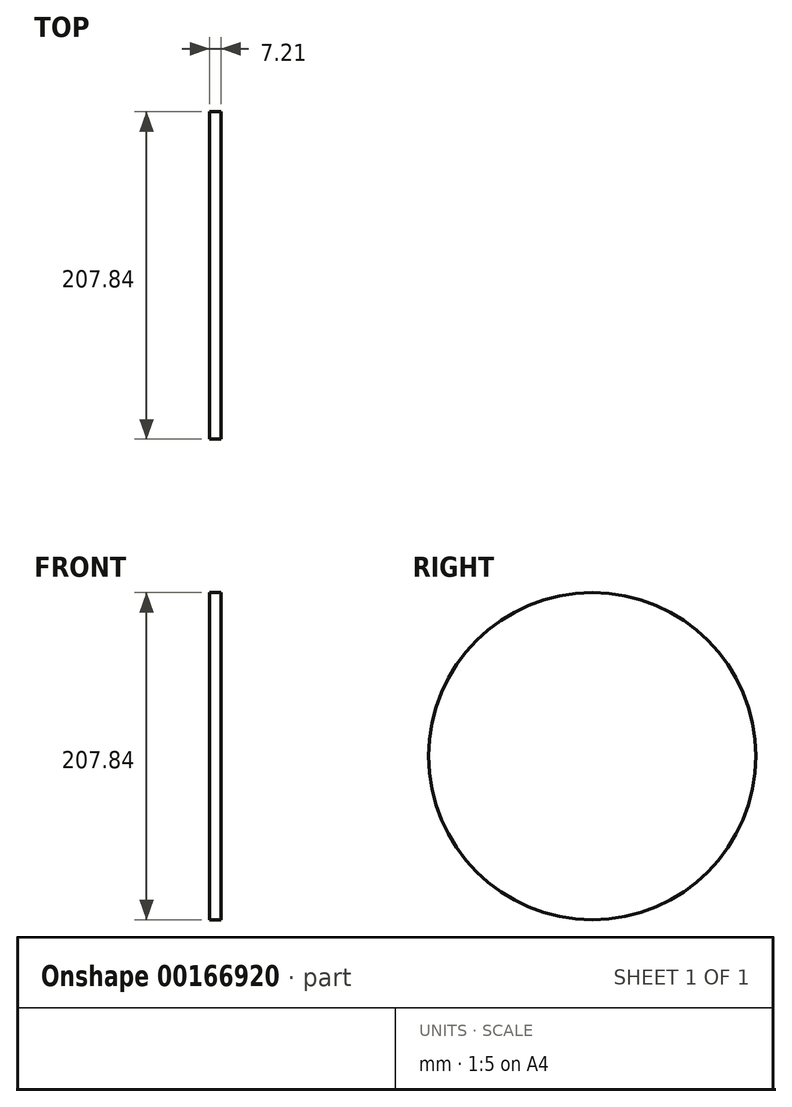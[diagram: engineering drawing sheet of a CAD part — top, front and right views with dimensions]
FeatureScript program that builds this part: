
annotation { "Feature Type Name" : "Feature", "Feature Type Description" : "" }
export const myFeature = defineFeature(function(context is Context, id is Id, definition is map)
    precondition{}
    {
        {
            var Q0;
            Q0=qCreatedBy(makeId("Right.planeOp"),FACE);
            var sketch = newSketch(context, id + "F0", { "sketchPlane" : qUnion([Q0])});
            skLineSegment(sketch, "E0", {"start": v(0, -129.27) * mm, "end": v(0, 113.16) * mm, "construction": true});
            skCircle(sketch, "E1", {"center": v(0, 0) * mm, "radius": 43 * mm, "construction": true});
            skCircle(sketch, "E2", {"center": v(0, 0) * mm, "radius": 25.5 * mm});
            skCircle(sketch, "E3", {"center": v(0, 0) * mm, "radius": 101.13 * mm, "construction": true});
            skLineSegment(sketch, "E4", {"start": v(0, 101.13) * mm, "end": v(78.11, 101.13) * mm, "construction": true});
            skLineSegment(sketch, "E5", {"start": v(0, 101.13) * mm, "end": v(-75.4, 101.13) * mm, "construction": true});
            skArc(sketch, "E6", {"start": v(-3.48, 98.58) * mm, "mid": v(-1.95, 97.28) * mm, "end": v(0, 96.82) * mm});
            skLineSegment(sketch, "E7", {"start": v(-51.83, 105.15) * mm, "end": v(64.83, 105.15) * mm, "construction": true});
            skLineSegment(sketch, "E8", {"start": v(5.5, 110.2) * mm, "end": v(5.5, 67.32) * mm, "construction": true});
            skPoint(sketch, "E9.orphan", {"position": v(5.5, 105.15) * mm});
            skLineSegment(sketch, "E10", {"start": v(-10.46, 93.48) * mm, "end": v(12.24, 110.09) * mm, "construction": true});
            skLineSegment(sketch, "E11", {"start": v(5.5, 105.15) * mm, "end": v(-5, 101.47) * mm, "construction": true});
            skArc(sketch, "E12", {"start": v(-5, 101.47) * mm, "mid": v(-4.37, 100.02) * mm, "end": v(-3.55, 98.68) * mm});
            skLineSegment(sketch, "E13", {"start": v(-5, 101.47) * mm, "end": v(-5.41, 102.65) * mm});
            skLineSegment(sketch, "E14", {"start": v(21.98, 100.38) * mm, "end": v(-19.96, 100.38) * mm, "construction": true});
            skLineSegment(sketch, "E15", {"start": v(-11.89, 114.56) * mm, "end": v(-11.89, 84.6) * mm, "construction": true});
            skLineSegment(sketch, "E16", {"start": v(0, 0) * mm, "end": v(-8.68, 137.98) * mm, "construction": true});
            skArc(sketch, "E17.trimOffspring", {"start": v(-5.41, 102.65) * mm, "mid": v(-5.64, 103.21) * mm, "end": v(-5.91, 103.75) * mm});
            skLineSegment(sketch, "E18", {"start": v(-11.89, 100.38) * mm, "end": v(-6.59, 104.74) * mm, "construction": true});
            skLineSegment(sketch, "E19", {"start": v(-11.89, 100.38) * mm, "end": v(-5.41, 102.65) * mm, "construction": true});
            skPoint(sketch, "E20.orphan", {"position": v(-6.59, 104.74) * mm});
            skLineSegment(sketch, "E21", {"start": v(0, 0) * mm, "end": v(6.53, 104.34) * mm, "construction": true});
            skCircle(sketch, "E22", {"center": v(-43, 0) * mm, "radius": 5.25 * mm});
            skCircle(sketch, "E23.1.0", {"center": v(0, -43) * mm, "radius": 5.25 * mm});
            skCircle(sketch, "E23.2.0", {"center": v(43, 0) * mm, "radius": 5.25 * mm});
            skCircle(sketch, "E23.3.0", {"center": v(0, 43) * mm, "radius": 5.25 * mm});
            skArc(sketch, "E24", {"start": v(-3.55, 98.68) * mm, "mid": v(-3.51, 98.63) * mm, "end": v(-3.48, 98.58) * mm});
            skCircle(sketch, "E25", {"center": v(0, 0) * mm, "radius": 103.92 * mm});
            skArc(sketch, "E26.MirrorCS", {"start": v(3.48, 98.58) * mm, "mid": v(1.95, 97.28) * mm, "end": v(0, 96.82) * mm});
            skArc(sketch, "E27.MirrorCS", {"start": v(5, 101.47) * mm, "mid": v(4.37, 100.02) * mm, "end": v(3.55, 98.68) * mm});
            skArc(sketch, "E28.MirrorCS", {"start": v(3.55, 98.68) * mm, "mid": v(3.51, 98.63) * mm, "end": v(3.48, 98.58) * mm});
            skArc(sketch, "E29.MirrorCS", {"start": v(5.41, 102.65) * mm, "mid": v(5.64, 103.21) * mm, "end": v(5.91, 103.75) * mm});
            skLineSegment(sketch, "E30.MirrorCS", {"start": v(5, 101.47) * mm, "end": v(5.41, 102.65) * mm});
            skSolve(sketch);
        }
        {
            var Q0;
            Q0=sQuery(id+"F0.wireOp",EDGE,"E25");
            extrude(context, id + "F1", {"bodyType" : ToolBodyType.SURFACE, "surfaceEntities" : qUnion([Q0]), "depth" : 7.2 * mm});
        }
    });
